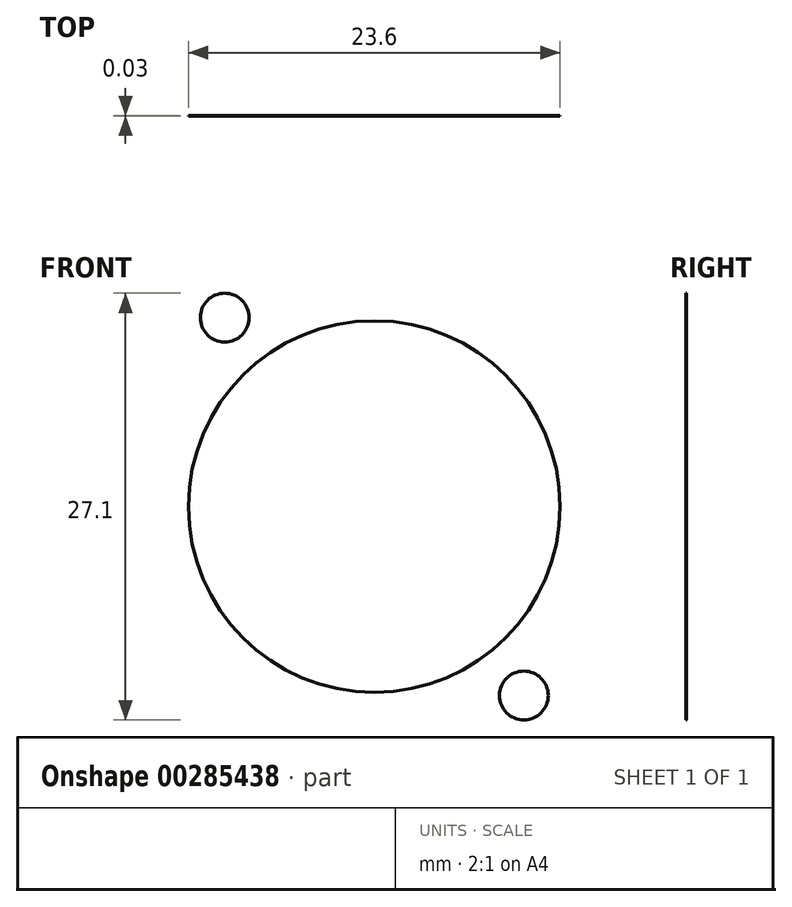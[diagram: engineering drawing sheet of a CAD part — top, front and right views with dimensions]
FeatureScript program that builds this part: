
annotation { "Feature Type Name" : "Feature", "Feature Type Description" : "" }
export const myFeature = defineFeature(function(context is Context, id is Id, definition is map)
    precondition{}
    {
        {
            var Q0;
            Q0=qCreatedBy(makeId("Front.planeOp"),FACE);
            var sketch = newSketch(context, id + "F0", { "sketchPlane" : qUnion([Q0])});
            skCircle(sketch, "E0", {"center": v(0, 0) * mm, "radius": 11.8 * mm});
            skCircle(sketch, "E1", {"center": v(-9.5, 12) * mm, "radius": 1.55 * mm});
            skCircle(sketch, "E2", {"center": v(9.5, -12) * mm, "radius": 1.55 * mm});
            skLineSegment(sketch, "E3.bottom", {"start": v(-9.83, 15.5) * mm, "end": v(9.83, 15.5) * mm, "construction": true});
            skLineSegment(sketch, "E3.top", {"start": v(-9.83, -15.5) * mm, "end": v(9.83, -15.5) * mm, "construction": true});
            skLineSegment(sketch, "E3.left", {"start": v(-13, 12.32) * mm, "end": v(-13, -12.32) * mm, "construction": true});
            skLineSegment(sketch, "E3.right", {"start": v(13, 12.32) * mm, "end": v(13, -12.32) * mm, "construction": true});
            skPoint(sketch, "E4.visualSharp", {"position": v(-13, 15.5) * mm});
            skArc(sketch, "E4.filletArc", {"start": v(-9.83, 15.5) * mm, "mid": v(-12.07, 14.56) * mm, "end": v(-13, 12.32) * mm, "construction": true});
            skPoint(sketch, "E5.visualSharp", {"position": v(13, 15.5) * mm});
            skArc(sketch, "E5.filletArc", {"start": v(13, 12.32) * mm, "mid": v(12.07, 14.56) * mm, "end": v(9.83, 15.5) * mm, "construction": true});
            skPoint(sketch, "E6.visualSharp", {"position": v(13, -15.5) * mm});
            skArc(sketch, "E6.filletArc", {"start": v(9.83, -15.5) * mm, "mid": v(12.07, -14.56) * mm, "end": v(13, -12.32) * mm, "construction": true});
            skPoint(sketch, "E7.visualSharp", {"position": v(-13, -15.5) * mm});
            skArc(sketch, "E7.filletArc", {"start": v(-13, -12.32) * mm, "mid": v(-12.07, -14.56) * mm, "end": v(-9.83, -15.5) * mm, "construction": true});
            skSolve(sketch);
        }
        {
            var Q0;
            Q0 = qSketchRegion(id + "F0", true);
            extrude(context, id + "F1", {"entities" : qUnion([Q0]), "depth" : 0.03 * mm});
        }
    });
